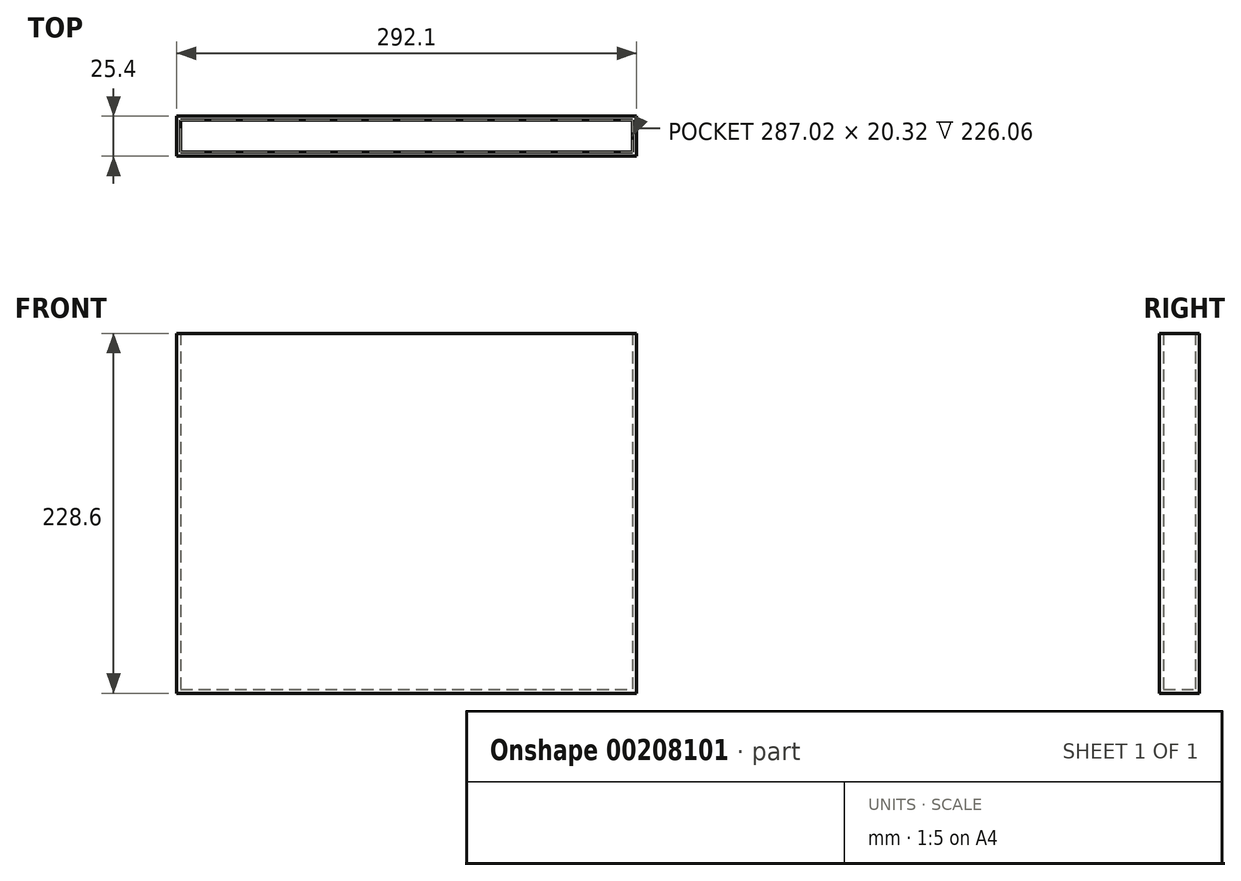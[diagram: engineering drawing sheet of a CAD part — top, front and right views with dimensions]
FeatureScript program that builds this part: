
annotation { "Feature Type Name" : "Feature", "Feature Type Description" : "" }
export const myFeature = defineFeature(function(context is Context, id is Id, definition is map)
    precondition{}
    {
        {
            var Q0;
            Q0=qCreatedBy(makeId("Front.planeOp"),FACE);
            var sketch = newSketch(context, id + "F0", { "sketchPlane" : qUnion([Q0])});
            skLineSegment(sketch, "E0.bottom", {"start": v(-146.05, 114.3) * mm, "end": v(146.05, 114.3) * mm});
            skLineSegment(sketch, "E0.top", {"start": v(-146.05, -114.3) * mm, "end": v(146.05, -114.3) * mm});
            skLineSegment(sketch, "E0.left", {"start": v(-146.05, 114.3) * mm, "end": v(-146.05, -114.3) * mm});
            skLineSegment(sketch, "E0.right", {"start": v(146.05, 114.3) * mm, "end": v(146.05, -114.3) * mm});
            skSolve(sketch);
        }
        {
            var Q0;
            Q0=makeQuery(id+"F0.imprint","IMPRINT",FACE,{"disambiguationData":[TD([[makeQuery(id+"F0.imprint","IMPRINT",EDGE,{"derivedFrom":sQuery(id+"F0.wireOp",EDGE,"E0.bottom")}),-1.0]])]});
            extrude(context, id + "F1", {"entities" : qUnion([Q0]), "depth" : 25.4 * mm});
        }
        {
            var Q0;
            Q0=makeQuery(id+"F1.opExtrude","SWEPT_FACE",FACE,{"disambiguationData":[OSD([sQuery(id+"F0.wireOp",EDGE,"E0.bottom")])]});
            var sketch = newSketch(context, id + "F2", { "sketchPlane" : qUnion([Q0])});
            skLineSegment(sketch, "E1.bottom", {"start": v(-140.4, -17.11) * mm, "end": v(139, -17.11) * mm});
            skLineSegment(sketch, "E1.top", {"start": v(-140.4, -8.73) * mm, "end": v(139, -8.73) * mm});
            skLineSegment(sketch, "E1.left", {"start": v(-140.4, -17.11) * mm, "end": v(-140.4, -8.73) * mm});
            skLineSegment(sketch, "E1.right", {"start": v(139, -17.11) * mm, "end": v(139, -8.73) * mm});
            skSolve(sketch);
        }
        {
            var Q0;
            Q0=makeQuery(id+"F1.opExtrude","SWEPT_FACE",FACE,{"disambiguationData":[OSD([sQuery(id+"F0.wireOp",EDGE,"E0.bottom")])]});
            shell(context, id + "F3", {"entities" : qUnion([Q0]), "thickness" : 2.54 * mm});
        }
    });
